# Revit family: Sanitary_Basins_Sanindusa_New-WC-Care-Washbasin
name_source: partatom
category: Plumbing Fixtures
revit_build: Autodesk Revit 2018 (Build: 20170223_1515(x64)
units: mm (PartAtom-declared; Revit-internal decimal feet)

## family parameters
Always vertical = Yes
Cut with Voids When Loaded = No
OmniClass Number = 23.45.00.00
OmniClass Title = Sanitary, Laundry, and Cleaning Equipment
Part Type = Normal
Room Calculation Point = No
Round Connector Dimension = Use Diameter
Shared = No
Work Plane-Based = Yes

## types (1)
- SanindusaLavatório
    AssetType = Fixed
    Category = Pr_40_20_96_18: Counter top wash basins
    CodePerformance = EN 14688:2015 CL 15
    Color = white
    Constituents = 48011U-chromed embellishment ring (included), 42902-Pneumatic fixation for washbasin 65 New Wccare (not included), 4V9211-Universal tic tac pop up waste(not included) , 4V9411-Universal tic tac pop up waste with little ABS mirror(not included) , 4V9111-Universal tic tac pop up waste with big round mirror(not included)
    Cost = 0 $
    Default Elevation = 1219 mm
    Description = wall-hung basin
    DrainSize = 47 mm  [stored 0.154199 ft]
    Edition number = 1
    Features = Installation wall-mounted. Glazed on all sides. Not rectified. Ergonomic shape adapted to the handicapped.
Front cutout for an easy approach to the basin. 
Armrest on upper surface.
Wide side flaps for safe and comfortable armrest. 
Shape of the side edges for easy grip, helping the user's movement.
Reduced height of the basin that allows the approach to the washbasin of persons in wheelchairs. 
lower setting plane of the mixer. Not rectified. Compatible with taps with and without pop up waste.
    Finish = gloss
    InstallationDate = 1900-12-31T23:59:59
    Manufacturer = Sanindusa
    ManufacturerName = Sanindusa
    ManufacturerURL = www.tec.sanindusa.pt
    Material = vitreous china
    ModelNumber = 129320004
    ModelReference = New Wccare
    Name = new wccare 65x58 washbasin
    NominalHeight = 160 mm  [stored 0.524934 ft]
    NominalLength = 652 mm  [stored 2.13911 ft]
    NominalWidth = 580 mm  [stored 1.90289 ft]
    Product Guid = 56db1b76-d12e-49b4-903a-c24ba35559ea
    Product data url = https://bimobject.com
    ProductInformation = https://www.tec.sanindusa.pt
    ProductionYear = 2017
    Shape = rectangular
    Size = 65x58
    SpilloverLevel = 72 mm  [stored 0.23622 ft]
    URL = www.tec.sanindusa.pt
    Uniclass2015Code = Pr_40_20_96_18
    Uniclass2015Title = Counter top wash basins
    Uniclass2015Version = Products v1.6
    Version = 2
    WarrantyDescription = https://www.tec.sanindusa.pt
    WarrantyDurationParts = 5
    WarrantyDurationUnit = year
    WarrantyStartDate = 1900-12-31T23:59:59
1900-12-31T23:59:59
    WashHandBasinMounting = wallhung
    WashHandBasinType = other
    Weight = 17.74 kg

note: [stored X ft] marks values corroborated as IEEE doubles in the binary element streams (Revit-internal decimal feet)

## geometry (parser evidence)
native form markers: Sweep x7
no freeform markers — native parametric forms only
